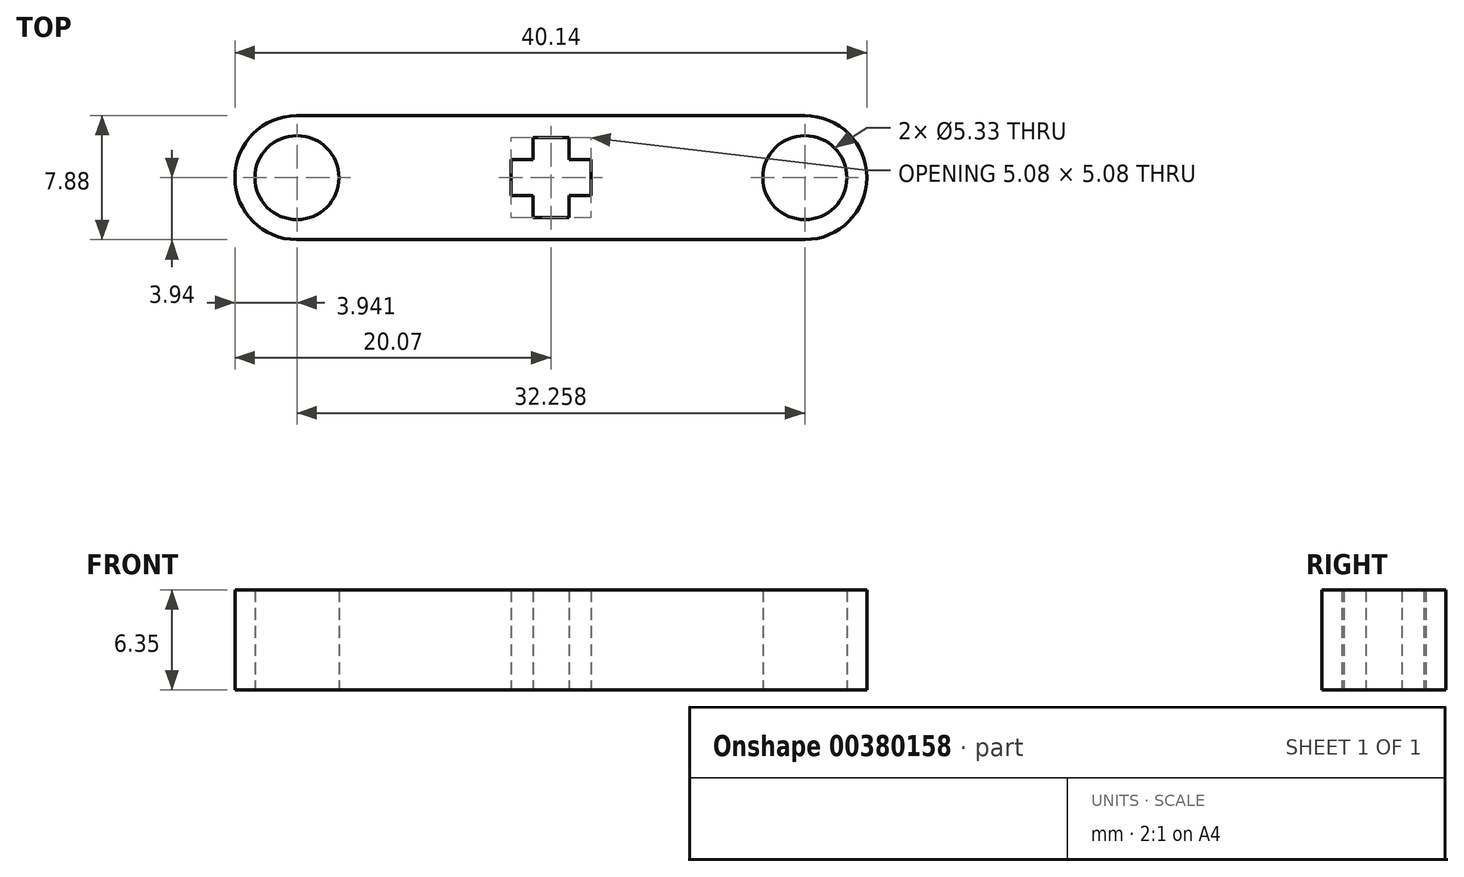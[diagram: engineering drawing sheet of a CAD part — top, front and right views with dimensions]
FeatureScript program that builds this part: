
annotation { "Feature Type Name" : "Feature", "Feature Type Description" : "" }
export const myFeature = defineFeature(function(context is Context, id is Id, definition is map)
    precondition{}
    {
        {
            var Q0;
            Q0=qCreatedBy(makeId("Top.planeOp"),FACE);
            var sketch = newSketch(context, id + "F0", { "sketchPlane" : qUnion([Q0]), "disableImprinting" : false});
            skLineSegment(sketch, "E0.bottom", {"start": v(16.13, -3.94) * mm, "end": v(-16.14, -3.94) * mm});
            skLineSegment(sketch, "E0.top", {"start": v(16.13, 3.94) * mm, "end": v(-16.14, 3.94) * mm});
            skLineSegment(sketch, "E0.left", {"start": v(20.07, 0) * mm, "end": v(20.07, 0) * mm});
            skLineSegment(sketch, "E0.right", {"start": v(-20.07, -0.01) * mm, "end": v(-20.07, 0.01) * mm});
            skPoint(sketch, "E0.middle", {"position": v(0, 0) * mm});
            skCircle(sketch, "E1", {"center": v(-16.13, 0) * mm, "radius": 2.67 * mm});
            skCircle(sketch, "E2.MirrorC", {"center": v(16.13, 0) * mm, "radius": 2.67 * mm});
            skLineSegment(sketch, "E3", {"start": v(0, 2.54) * mm, "end": v(-1.14, 2.54) * mm});
            skLineSegment(sketch, "E4", {"start": v(-1.14, 2.54) * mm, "end": v(-1.14, 1.14) * mm});
            skLineSegment(sketch, "E5", {"start": v(-1.14, 1.14) * mm, "end": v(-2.54, 1.14) * mm});
            skLineSegment(sketch, "E6", {"start": v(-2.54, 1.14) * mm, "end": v(-2.54, 0) * mm});
            skLineSegment(sketch, "E7.MirrorCS", {"start": v(1.14, 1.14) * mm, "end": v(2.54, 1.14) * mm});
            skLineSegment(sketch, "E8.MirrorCS", {"start": v(1.14, 2.54) * mm, "end": v(1.14, 1.14) * mm});
            skLineSegment(sketch, "E9.MirrorCS", {"start": v(2.54, 1.14) * mm, "end": v(2.54, 0) * mm});
            skLineSegment(sketch, "E10.MirrorCS", {"start": v(0, 2.54) * mm, "end": v(1.14, 2.54) * mm});
            skLineSegment(sketch, "E11.MirrorCS", {"start": v(0, -2.54) * mm, "end": v(1.14, -2.54) * mm});
            skLineSegment(sketch, "E12.MirrorCS", {"start": v(1.14, -2.54) * mm, "end": v(1.14, -1.14) * mm});
            skLineSegment(sketch, "E13.MirrorCS", {"start": v(1.14, -1.14) * mm, "end": v(2.54, -1.14) * mm});
            skLineSegment(sketch, "E14.MirrorCS", {"start": v(-1.14, -2.54) * mm, "end": v(-1.14, -1.14) * mm});
            skLineSegment(sketch, "E15.MirrorCS", {"start": v(0, -2.54) * mm, "end": v(-1.14, -2.54) * mm});
            skLineSegment(sketch, "E16.MirrorCS", {"start": v(-1.14, -1.14) * mm, "end": v(-2.54, -1.14) * mm});
            skLineSegment(sketch, "E17.MirrorCS", {"start": v(2.54, -1.14) * mm, "end": v(2.54, 0) * mm});
            skLineSegment(sketch, "E18.MirrorCS", {"start": v(-2.54, -1.14) * mm, "end": v(-2.54, 0) * mm});
            skPoint(sketch, "E19.visualSharp", {"position": v(-20.07, 3.94) * mm});
            skArc(sketch, "E19.filletArc", {"start": v(-16.14, 3.94) * mm, "mid": v(-18.92, 2.79) * mm, "end": v(-20.07, 0.01) * mm});
            skPoint(sketch, "E20.visualSharp", {"position": v(-20.07, -3.94) * mm});
            skArc(sketch, "E20.filletArc", {"start": v(-20.07, -0.01) * mm, "mid": v(-18.92, -2.79) * mm, "end": v(-16.14, -3.94) * mm});
            skPoint(sketch, "E21.visualSharp", {"position": v(20.07, 3.94) * mm});
            skArc(sketch, "E21.filletArc", {"start": v(20.07, 0) * mm, "mid": v(18.91, 2.78) * mm, "end": v(16.13, 3.94) * mm});
            skPoint(sketch, "E22.visualSharp", {"position": v(20.07, -3.94) * mm});
            skArc(sketch, "E22.filletArc", {"start": v(16.13, -3.94) * mm, "mid": v(18.91, -2.78) * mm, "end": v(20.07, 0) * mm});
            skSolve(sketch);
        }
        {
            var Q0;
            Q0=makeQuery(id+"F0.imprint","IMPRINT",FACE,{"disambiguationData":[TD([[makeQuery(id+"F0.imprint","IMPRINT",EDGE,{"derivedFrom":sQuery(id+"F0.wireOp",EDGE,"E0.bottom")}),-1.0]])]});
            extrude(context, id + "F1", {"entities" : qUnion([Q0]), "depth" : 6.35 * mm});
        }
    });
